FCSTD DOCUMENT  (FreeCAD 0.20R29177 +426 (Git))
Label: Params
License: All rights reserved
LicenseURL: http://en.wikipedia.org/wiki/All_rights_reserved
objects: Spreadsheet::Sheet×1

FEATURE [Spreadsheet::Sheet] Spreadsheet  label="Params"
  cells = A1=DriveWheelWidth; B1(DriveWheelWidth)=10; D1=PlywoodThickness; E1(PlywoodThickness)=18.5; A2=DriveWheelMajorDiameter; B2(DriveWheelMajorDiameter)=52; D2=ExtensionArmCenterOffset; E2(ExtensionArmCenterOffset)=23; A3=DriveWheelCrown; B3(DriveWheelCrown)=2; D3=SheetMetalThickness; E3(SheetMetalThickness)=2.656; A4=DriveWheelTireThickness; B4(DriveWheelTireThickness)=3; D4=CeilingPlateDiameter; E4(CeilingPlateDiameter)=463; A6=DriveUnitAngle; B6(DriveUnitAngle)=30; D6=TableRollerMountHoleSpacing; E6(TableRollerMountHoleSpacing)=24; A7=DriveRadius; B7(DriveRadius)=280; D7=TableRollerMountHoleOffset; E7(TableRollerMountHoleOffset)=12; A8=DriveAdjMiddleOffset; B8(DriveAdjMiddleOffset)=90; D8=TableRollerDriveSupportRadius; E8(TableRollerDriveSupportRadius)=218; A9=RotationDriveOffset; B9(RotationDriveOffset)=29; D9=TableRollerSideRadius; E9(TableRollerSideRadius)=164; A10=FrontSkateOffset; B10(FrontSkateOffset)=350; D10=TableRollerDriveSupportAngle; E10(TableRollerDriveSupportAngle)=13.5; A11=RearSkateOffset; B11(RearSkateOffset)=150; D11=TableRollerSideAngle; E11(TableRollerSideAngle)=20; A13=CablePulleyDiameter; B13(CablePulleyDiameter)=120; D13=RoomWidth; E13(RoomWidth)=3650; D14=RoomLength; E14(RoomLength)=3650; A15=ExtensionDriverOffsetX; B15(ExtensionDriverOffsetX)=100; D15=RoomHeight; E15(RoomHeight)=2440; A16=ExtensionDriverOffsetY; B16(ExtensionDriverOffsetY)=-36
